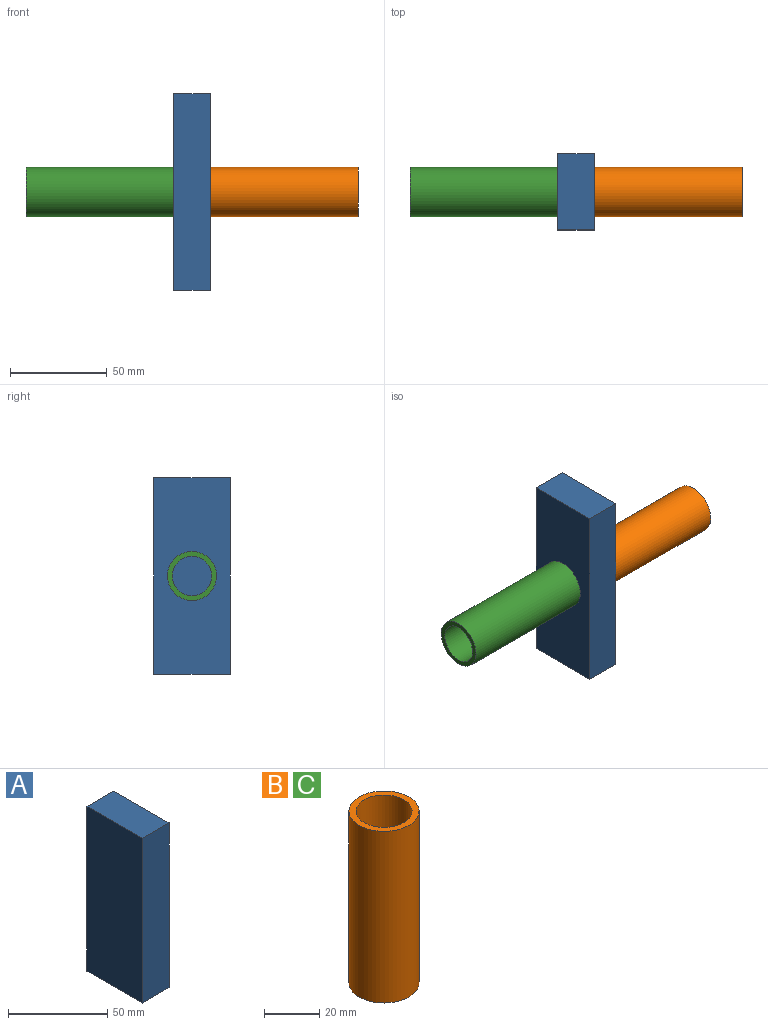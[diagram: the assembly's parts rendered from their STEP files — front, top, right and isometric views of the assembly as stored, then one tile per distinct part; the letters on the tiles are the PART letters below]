
ASSEMBLY  parts=3 mates=2
PART A: 6 faces, bbox 19x39.4x101.6 mm
  f0: plane 39.37x19.04mm, normal (0,0,1), area 749.6mm2, adj f1,f3,f4,f5
  f1: plane 101.55x39.37mm, normal (-1,0,0), area 3998.1mm2, adj f0,f2,f4,f5
  f2: plane 39.37x19.04mm, normal (0,0,-1), area 749.6mm2, adj f1,f3,f4,f5
  f3: plane 101.55x39.37mm, normal (1,0,0), area 3998.1mm2, adj f0,f2,f4,f5
  f4: plane 101.55x19.04mm, normal (0,-1,0), area 1933.6mm2, adj f0,f1,f2,f3
  f5: plane 101.55x19.04mm, normal (0,1,0), area 1933.6mm2, adj f0,f1,f2,f3
PART B: 4 faces, bbox 25.4x25.4x76.2 mm
  f0: cylinder r=10.16mm len=76.2mm, axis (0,0,-1), area 4864.4mm2, adj f2,f3
  f1: cylinder r=12.7mm len=76.2mm, axis (0,0,-1), area 6080.5mm2, adj f2,f3
  f2: plane 25.4x25.4mm, normal (0,0,1), area 182.4mm2, adj f0,f1
  f3: plane 25.4x25.4mm, normal (0,0,-1), area 182.4mm2, adj f0,f1
PART C: same geometry as B
PLACE A t=(-29.88,0.23,-1.86)mm
PLACE B rot(axis=(0,1,0),90deg) t=(-20.36,-19.46,-3.31)mm
PLACE C rot(axis=(0,-1,0),90deg) t=(-39.4,-19.46,-3.31)mm
MATE fastened C.f1 <-> A.f1  axis (1,0,0) through (-39.4,-19.46,-3.31)mm
MATE fastened B.f1 <-> A.f3  axis (-1,0,0) through (-20.36,-19.46,-3.31)mm
